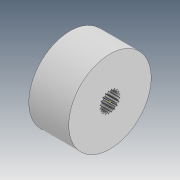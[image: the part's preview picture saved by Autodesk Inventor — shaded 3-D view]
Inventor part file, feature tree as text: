
AUTODESK INVENTOR PART (.ipt)
format: ipt  version: 2021 (Build 250183000, 183)  size: 270,336 bytes
history: native  units: in
note: dims shown in document units (in); Inventor stores cm internally (conversion verified against a paired STEP export)
features: sketch x5, extrude x3, other x2
ambient origin geometry x8: Origin, YZ Plane, XZ Plane, XY Plane, X Axis, Y Axis, Z Axis, Center Point
bodies: Body1 (feature_tree)
feature tree (10):
  other  "Sólido1"
  other  "Revolução1"
  extrude  "Extrusão1"  Depth=0.3858in
  extrude  "Extrusão2"  Depth=0.1378in
  extrude  "Extrusão3"  Depth=0.1909in
  sketch  "Esboço9"  dims[d35=0.1575in d36=0.189in d37=0.002in d38=0.002in d39=0.002in d40=0.1378in d41=0.0in d42=7.874in d44=360.0deg]
  sketch  "Esboço2"  dims[d0=0.374in d1=0.3858in]
  sketch  "Esboço3"  dims[d2=90.0deg d3=0.1378in]
  sketch  "Esboço4"  dims[d4=0.1909in d5=0.0in d6=0.3543in]
  sketch  "Esboço8"  dims[d7=0.0787in d8=0.0in]
